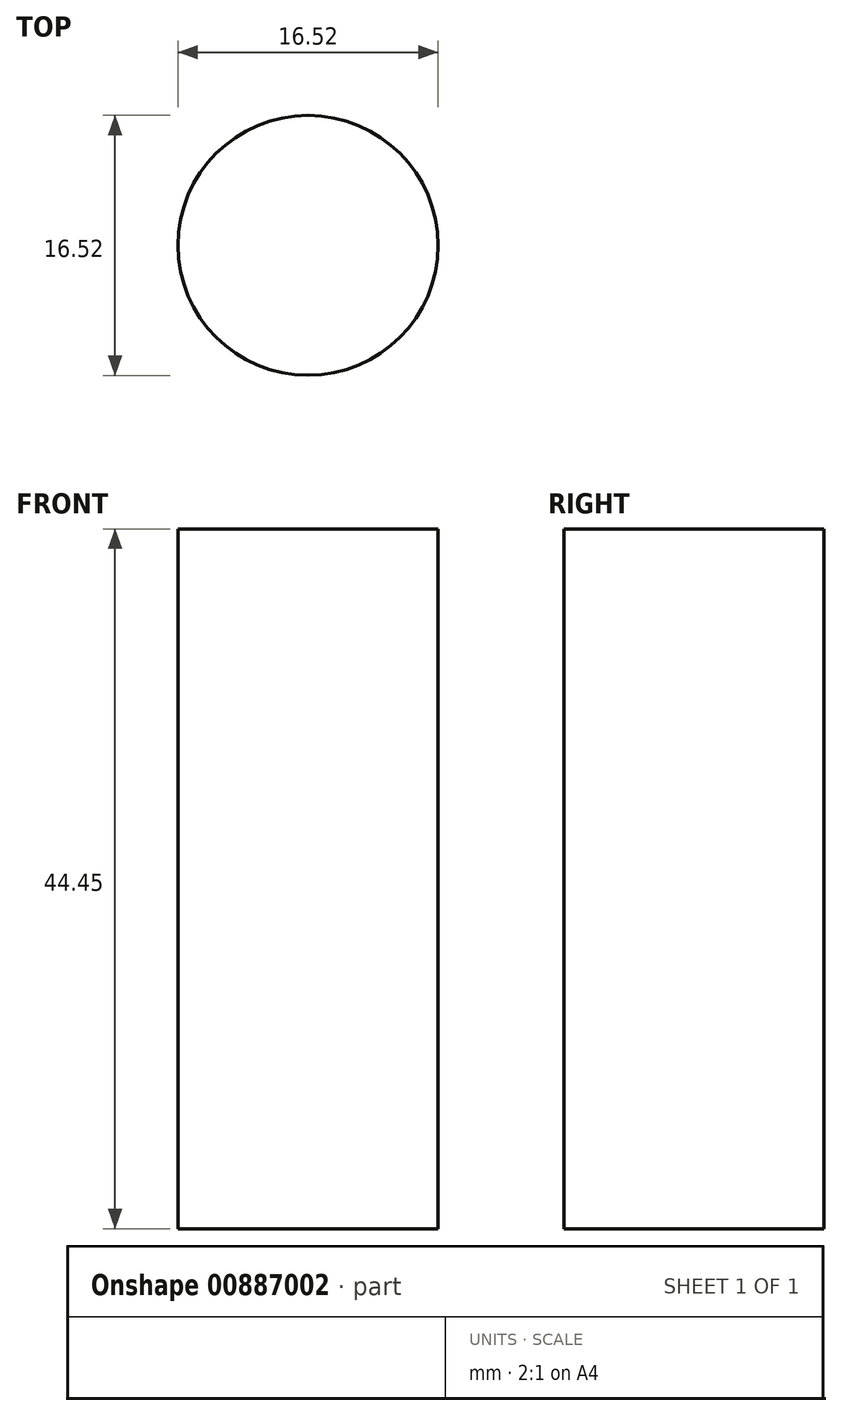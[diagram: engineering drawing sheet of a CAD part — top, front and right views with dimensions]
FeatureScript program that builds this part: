
annotation { "Feature Type Name" : "Feature", "Feature Type Description" : "" }
export const myFeature = defineFeature(function(context is Context, id is Id, definition is map)
    precondition{}
    {
        {
            var Q0;
            Q0=qCreatedBy(makeId("Top.planeOp"),FACE);
            var sketch = newSketch(context, id + "F0", { "sketchPlane" : qUnion([Q0])});
            skCircle(sketch, "E0", {"center": v(0, 0) * mm, "radius": 8.26 * mm});
            skSolve(sketch);
        }
        {
            var Q0;
            Q0=makeQuery(id+"F0.imprint","IMPRINT",FACE,{"disambiguationData":[TD([[makeQuery(id+"F0.imprint","IMPRINT",EDGE,{"derivedFrom":sQuery(id+"F0.wireOp",EDGE,"E0")}),1.0]])]});
            extrude(context, id + "F1", {"entities" : qUnion([Q0]), "depth" : 44.45 * mm, "offsetDistance" : 25.4 * mm});
        }
    });
